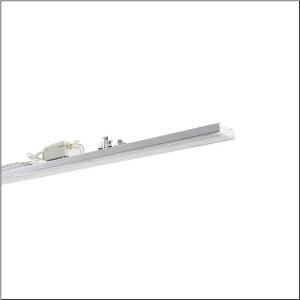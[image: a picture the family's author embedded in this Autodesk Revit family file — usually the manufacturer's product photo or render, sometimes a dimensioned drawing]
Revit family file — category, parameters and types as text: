
# Revit family: licross_r__21_recessed_ho_52tl18mn4e5m_adf3
name_source: partatom
category: Lighting Fixtures
units: mm (PartAtom-declared; Revit-internal decimal feet)

## family parameters
Cut with Voids When Loaded = No
Host = Face
Light Source = No
Part Type = Normal
Room Calculation Point = No
Round Connector Dimension = Use Diameter
Shared = No

## types (1)
- --- (1 x LED, 14940 lm, 83.1 W, 4000K)
    Apparent Load = 83 VA
    CIE Flux Codes = 75 94 99 100 100
    Color Rendering = 80
    Color Temperature = 4000K
    Default Elevation = 1800 mm
    Description = Licross® 21 Recessed HO, luminaire insert, of sheet steel, galvanised, coil coated, white, length: 1.500mm, width: 66mm, height: 67mm, LED rated luminous flux: 14.940lm, light colour: 840, control gear: ON/OFF Multilumen, with plug, 3-pole, with phase selection, mains connection: 220..240V, AC, 50/60Hz, rated input power: 83W, halogen-free wiring, primary light control with lens, of plastic, primary optical cover: cover, of PMMA, light emission: direct distribution, primary light characteristic: symmetric, protection rating (complete): IP40, insulation class (complete): insulation class I (protective earthing), certification: CE, ENEC, VDE, UKCA, protection symbol: D if used in an environment without relevant dust loads with corresponding accessories, impact resistance: IK06, permissible ambient temperature for indoor applications: -35..+30°C, corresponds to IFS (International Featured Standards) requirements for safety and quality in the food industry, reducing of maximum allowable ambient temperature of 5°C with ceiling mounting, LABS conformity tested according to VDMA 24364:2018-05, packaging unit: 1 piece
    Height = 58 mm
    Lamp = 1 x LED
    Lamp Light Flux = 14940 lm
    Lamp Power = 83.1 W
    Lamp count = 1
    Length = 1500 mm
    Luminous efficacy = 180 lm/W
    Manufacturer = Siteco
    ModVariant = No
    Model = 52TL18MN4E5M
    Mounting Place = Ceiling
    Mounting Type = Pendant
    Number of Poles = 1
    OnlyDefault = Yes
    Power Factor = 1
    Product Name = Licross® 21 Recessed HO
    Product group = luminaire insert
    ProductGroupID = 901
    Protection Class = Protection class I
    Protection Degree = IP 40
    RLX_Detail_Level = 1
    RLX_Emergency_Light_Flux = 0 lm
    RLX_Emergency_Type = 0
    RLX_Emergency_Type_DB = No
    RlxData = <blob elided: 22289 chars, md5=505c613c>
    Socket = socket
    Standby Power = 0 W
    System Light Flux = 14940 lm
    System Power = 83 W
    Type Comments = factory setting: luminous flux: 100 % | (A | C | E) | 195 mA
    Type Image = l_1296930.jpg
    URL = http://relux.com
    VarID = @adj_038113
    Voltage = 0 V
    Weight = 0.00 kg
    Width = 66 mm

## geometry (parser evidence)
native form markers: Blend x4, Sweep x13
no freeform markers — native parametric forms only
